# Revit family: Syke sofa
name_source: partatom
category: Furniture
revit_build: Autodesk Revit 2015 (Build: 20140606_1530(x64)
units: mm (PartAtom-declared; Revit-internal decimal feet)

## types (11) — shared parameters
Back support left = Syke backrest skewed : Length 100
Manufacturer = Isku Oy
Type Comments = Available as antimicrobial
URL = www.isku.fi

## per-type parameters (varying)
| type | Back support corner | Back support right | Left armrest | Left back support | Right armrest | Right back support | Seat |
| Syke width 200 with armrests | No | Syke backrest skewed : Length 100 | Yes | Yes | Yes | Yes | syke seat : Seat 200x85 |
| Syke width 200 with left armrest | No | Syke backrest skewed : Length 100 | Yes | Yes | No | Yes | syke seat : Seat 200x85 |
| Syke width 200 with right armrest | No | Syke backrest skewed : Length 100 | No | Yes | Yes | Yes | syke seat : Seat 200x85 |
| Syke width 200 no armrest | No | Syke backrest skewed : Length 100 | No | Yes | No | Yes | syke seat : Seat 200x85 |
| Syke width 150 with right armrest | No | Syke backrest skewed : Length 50 | No | Yes | Yes | Yes | syke seat : Seat 150x85 |
| Syke width 150 no armrest | No | Syke backrest skewed : Length 50 | No | Yes | No | Yes | syke seat : Seat 150x85 |
| Syke width 150 with armrests | No | Syke backrest skewed : Length 50 | Yes | Yes | Yes | Yes | syke seat : Seat 150x85 |
| Syke width 150 with left armrest | No | Syke backrest skewed : Length 50 | Yes | Yes | No | Yes | syke seat : Seat 150x85 |
| Syke width 100 with back support | No | Syke backrest skewed : Length 50 | No | Yes | No | No | syke seat : Seat 100x85 |
| Syke width 100 no back support | No | Syke backrest skewed : Length 50 | No | No | No | No | syke seat : Seat 100x85 |
| Syke corner | Yes | Syke backrest skewed : Length 50 | No | No | No | No | syke seat : Seat 85x85 |

## geometry (parser evidence)
native form markers: Blend x4, Sweep x27
no freeform markers — native parametric forms only
